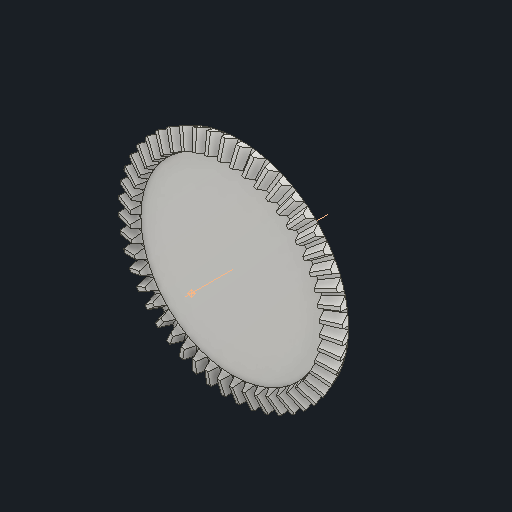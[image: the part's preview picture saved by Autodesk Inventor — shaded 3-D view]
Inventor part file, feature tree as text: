
AUTODESK INVENTOR PART (.ipt)
format: ipt  version: 2022 (Build 260153000, 153)  size: 709,120 bytes
history: native  units: mm
features: other x24, loft x2, pattern_circular x2, sketch x1
ambient origin geometry x6: Origin, XZ Plane, X Axis, Y Axis, Z Axis, Center Point
bodies: Solid1 (feature_tree)
feature tree (29):
  other  "Top Point"
  other  "Mesh Plane2"
  other  "Teeth Body"
  other  "Start Point"
  other  "Tooth Plane"
  other  "Start Sketch"
  other  "End Point"
  other  "3D Sketch Right"
  other  "End Plane Right"
  loft  "Loft Right"
  pattern_circular  "Circular Pattern Right"  [2 undecoded]
  other  "3D Sketch Left"
  other  "End Plane Left"
  loft  "Loft Left"
  pattern_circular  "Circular Pattern Left"  [2 undecoded]
  other  "Fix Body"
  other  "Mesh Plane"
  other  "Top Plane"
  other  "Teeth Body Sketch"
  other  "End Plane"
  other  "End Sketch"
  other  "Helical Curve Left"
  other  "End Sketch Left"
  other  "Body Sketch"
  sketch  "Sketch6"  dims[d0=120.0mm d1=118.488225mm d2=122.536758mm d3=10.0mm d4=20.545674mm d5=90.0deg d7=59.301777mm d8=57.411626mm d9=142.839828mm d11=10.275mm d12=49.859192mm d15=48.270008mm d16=120.09553mm d17=0.0mm d18=90.0deg d19=0.0mm d20=90.0deg d21=480.0mm d22=360.0deg d26=351.677194mm d27=3.781698mm d28=120.0mm d29=-11.938871mm d30=49.859192mm d31=48.270008mm d32=120.09553mm d35=0.0mm d37=0.0mm d39=0.0mm d40=90.0deg d41=480.0mm d42=360.0deg d46=90.0deg d47=90.0deg d48=0.0mm d49=0.0mm d50=90.0deg d51=0.654498mm d52=0.0mm d53=0.0mm d54=0.0mm d56=19.079059mm d57=168.118244mm d58=160.308244mm d59=141.34888mm d60=134.782461mm d61=141.34888mm d62=134.782461mm d65=351.677194mm d66=31.5mm d67=120.0mm d68=-11.938871mm d69=3.781698mm d70=48.270008mm d71=120.09553mm d72=49.859192mm d73=134.782461mm d74=141.34888mm d75=0.0mm d77=0.0mm d79=0.0mm d80=90.0deg d81=480.0mm d82=360.0deg d84=10.0mm d85=20.0mm d86=20.0mm d87=10.0mm d88=0.0mm d89=0.0mm d90=90.0deg d91=90.0deg d92=90.0deg d93=90.0deg]
  other  "Srf1"
  other  "Helical Curve Right"
  other  "End Sketch Right"
  other  "Pitch Diameter"
note: 4 required parameter values undecoded (feature->parameter linkage not recoverable at this tier; creation-order binding heuristic only, values carry confidence <= 0.55)
